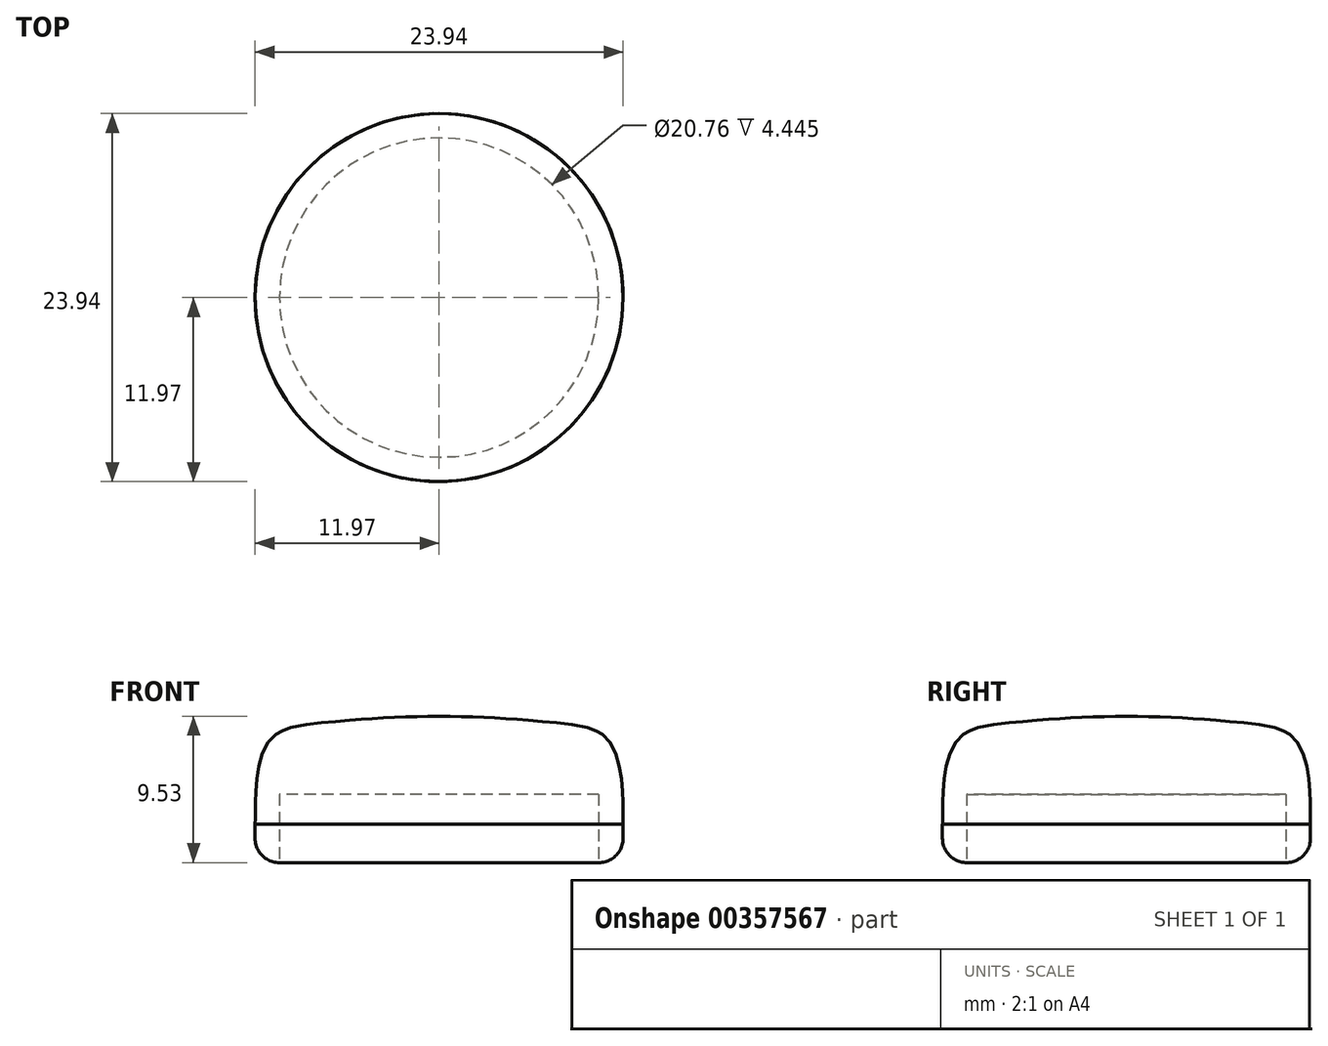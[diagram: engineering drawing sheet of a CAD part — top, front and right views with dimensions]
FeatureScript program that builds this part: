
annotation { "Feature Type Name" : "Feature", "Feature Type Description" : "" }
export const myFeature = defineFeature(function(context is Context, id is Id, definition is map)
    precondition{}
    {
        {
            var Q0;
            Q0=qCreatedBy(makeId("Top.planeOp"),FACE);
            var sketch = newSketch(context, id + "F0", { "sketchPlane" : qUnion([Q0])});
            skCircle(sketch, "E0", {"center": v(0, 0) * mm, "radius": 11.97 * mm});
            skSolve(sketch);
        }
        {
            var Q0;
            Q0=qCreatedBy(makeId("Top.planeOp"),FACE);
            var sketch = newSketch(context, id + "F1", { "sketchPlane" : qUnion([Q0])});
            skCircle(sketch, "E1", {"center": v(0, 0) * mm, "radius": 10.38 * mm});
            skSolve(sketch);
        }
        {
            var Q0;
            Q0=makeQuery(id+"F0.imprint","IMPRINT",FACE,{"disambiguationData":[TD([[makeQuery(id+"F0.imprint","IMPRINT",EDGE,{"derivedFrom":sQuery(id+"F0.wireOp",EDGE,"E0")}),1.0]])]});
            extrude(context, id + "F2", {"entities" : qUnion([Q0]), "depth" : 9.52 * mm});
        }
        {
            var Q0;
            Q0=makeQuery(id+"F1.imprint","IMPRINT",FACE,{"disambiguationData":[TD([[makeQuery(id+"F1.imprint","IMPRINT",EDGE,{"derivedFrom":sQuery(id+"F1.wireOp",EDGE,"E1")}),1.0]])]});
            extrude(context, id + "F3", {"entities" : qUnion([Q0]), "operationType" : NewBodyOperationType.REMOVE, "depth" : 4.44 * mm});
        }
        {
            var Q0;
            Q0=qCreatedBy(makeId("Front.planeOp"),FACE);
            var sketch = newSketch(context, id + "F4", { "sketchPlane" : qUnion([Q0])});
            skFitSpline(sketch, "E2", {"points": [v(0, 9.53) * mm, v(7.6, 9.1) * mm, v(10.95, 8.03) * mm, v(11.9, 4.78) * mm, v(11.97, 2.5) * mm], "startDerivative": vector(27.23, -0.3) * mm, "endDerivative": vector(0.2, -11.09) * mm});
            skLineSegment(sketch, "E3", {"start": v(11.97, 2.5) * mm, "end": v(12.48, 2.85) * mm});
            skLineSegment(sketch, "E4", {"start": v(12.48, 2.85) * mm, "end": v(12.34, 9.9) * mm});
            skLineSegment(sketch, "E5", {"start": v(12.34, 9.9) * mm, "end": v(0.5, 10.12) * mm});
            skLineSegment(sketch, "E6", {"start": v(0.5, 10.12) * mm, "end": v(0, 9.53) * mm});
            skSolve(sketch);
        }
        {
            var Q0;
            Q0=qCreatedBy(makeId("Front.planeOp"),FACE);
            var sketch = newSketch(context, id + "F5", { "sketchPlane" : qUnion([Q0])});
            skLineSegment(sketch, "E7", {"start": v(0, 0) * mm, "end": v(0, 12.3) * mm, "construction": true});
            skSolve(sketch);
        }
        {
            var Q0;
            Q0=makeQuery(id+"F4.imprint","IMPRINT",FACE,{"disambiguationData":[TD([[makeQuery(id+"F4.imprint","IMPRINT",EDGE,{"derivedFrom":sQuery(id+"F4.wireOp",EDGE,"E2")}),1.0]])]});
            var Q1;
            Q1 = qConstructionFilter(qBodyType(qCreatedBy(id + "F4" ,EDGE), BodyType.WIRE), ConstructionObject.NO);
            var Q2;
            Q2=sQuery(id+"F5.wireOp",EDGE,"E7");
            revolve(context, id + "F6", {"operationType" : NewBodyOperationType.REMOVE, "entities" : qUnion([Q0]), "surfaceEntities" : qUnion([Q1]), "axis" : qUnion([Q2]), "revolveType" : RevolveType.ONE_DIRECTION, "oppositeDirection" : true, "angle" : 350 * degree});
        }
        {
            var Q0;
            Q0 = qSketchRegion(id + "F4", true);
            var Q1;
            Q1=sQuery(id+"F5.wireOp",EDGE,"E7");
            revolve(context, id + "F7", {"operationType" : NewBodyOperationType.REMOVE, "entities" : qUnion([Q0]), "axis" : qUnion([Q1]), "revolveType" : RevolveType.ONE_DIRECTION, "angle" : 30 * degree});
        }
        {
            var Q0;
            Q0=makeQuery(id+"F2.opExtrude","CAP_EDGE",EDGE,{"disambiguationData":[OSD([sQuery(id+"F0.wireOp",EDGE,"E0")])],"isStart":true});
            fillet(context, id + "F8", {"entities" : qUnion([Q0]), "radius" : 1.59 * mm, "tangentPropagation" : true, "allowEdgeOverflow" : false});
        }
    });
